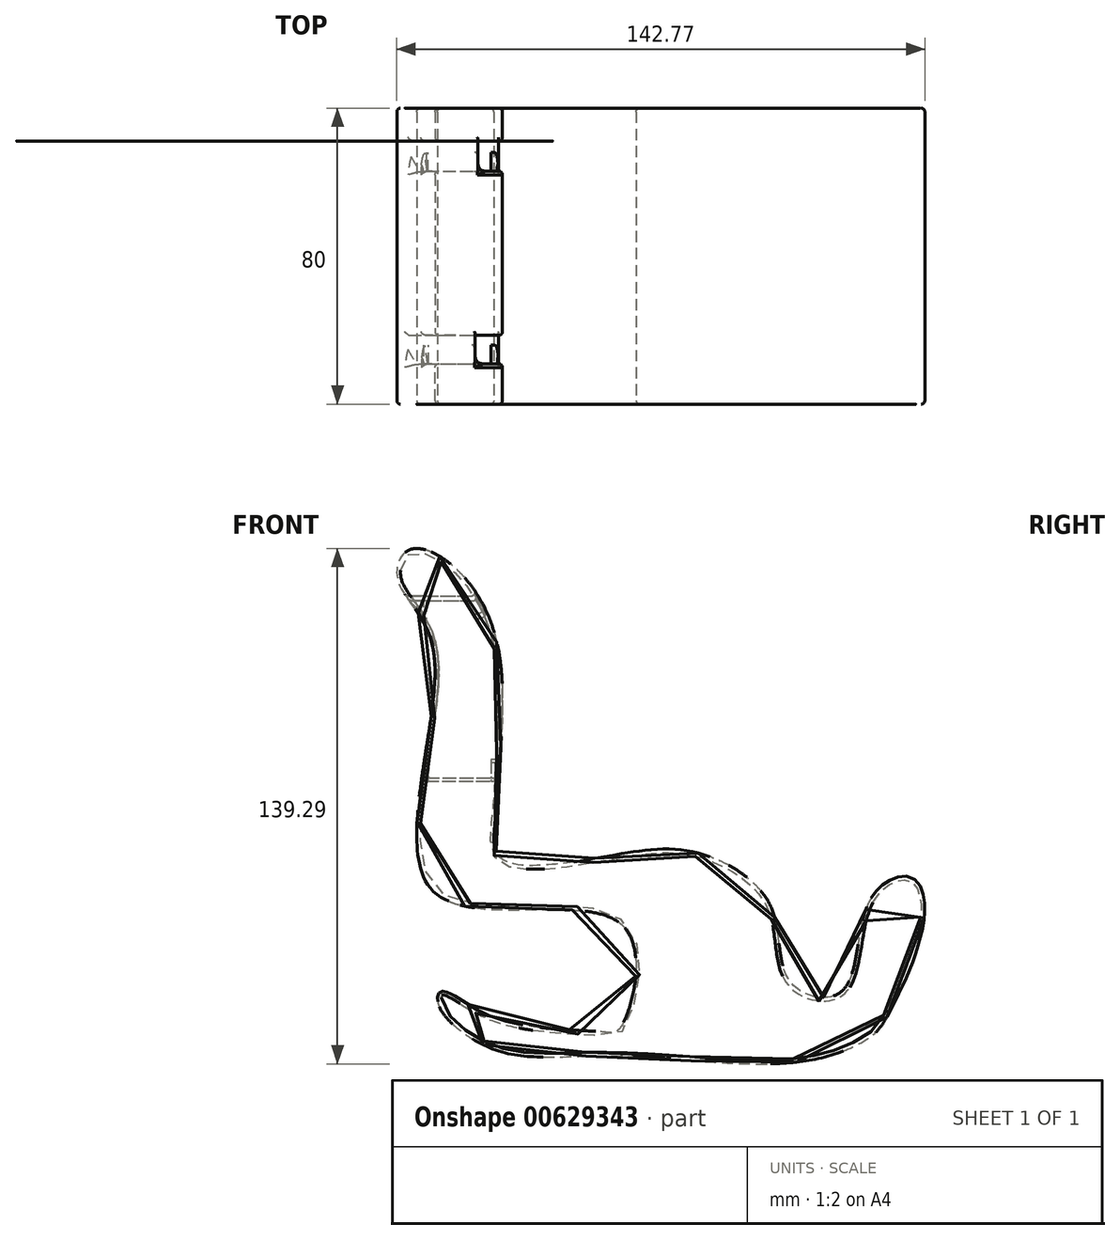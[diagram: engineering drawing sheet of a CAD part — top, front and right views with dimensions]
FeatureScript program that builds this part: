
annotation { "Feature Type Name" : "Feature", "Feature Type Description" : "" }
export const myFeature = defineFeature(function(context is Context, id is Id, definition is map)
    precondition{}
    {
        {
            var Q0;
            Q0=qCreatedBy(makeId("Front.planeOp"),FACE);
            var sketch = newSketch(context, id + "F0", { "sketchPlane" : qUnion([Q0])});
            skFitSpline(sketch, "E0", {"points": [v(60.46, -57.81) * mm, v(55.58, -63.5) * mm, v(36.46, -70.01) * mm, v(-14.39, -68.39) * mm, v(-45.3, -66.76) * mm, v(-60.77, -54.56) * mm, v(-59.95, -50.9) * mm, v(-46.12, -57.81) * mm, v(-16.42, -61.88) * mm, v(-11.54, -60.66) * mm, v(-11.14, -33) * mm, v(-61.99, -24.05) * mm, v(-61.99, 40.23) * mm, v(-71.75, 60.16) * mm, v(-68.9, 68.3) * mm, v(-57.1, 64.23) * mm, v(-44.9, 43.08) * mm, v(-44.09, 12.97) * mm, v(-45.3, -3.7) * mm, v(-43.68, -15.1) * mm, v(-14.39, -14.28) * mm, v(9.2, -13.47) * mm, v(29.14, -28.11) * mm, v(34.43, -48.45) * mm, v(48.26, -50.9) * mm, v(55.58, -26.9) * mm, v(66.56, -19.98) * mm, v(70.63, -30.55) * mm, v(60.46, -57.81) * mm]});
            skSolve(sketch);
        }
        {
            var Q0;
            Q0 = qSketchRegion(id + "F0", true);
            extrude(context, id + "F1", {"entities" : qUnion([Q0]), "endBound" : BoundingType.SYMMETRIC, "oppositeDirection" : true, "depth" : 80 * mm, "offsetDistance" : 25 * mm});
        }
        {
            var Q0;
            Q0=qCreatedBy(makeId("Right.planeOp"),FACE);
            var sketch = newSketch(context, id + "F2", { "sketchPlane" : qUnion([Q0])});
            skLineSegment(sketch, "E1.bottom", {"start": v(-29.09, 55.94) * mm, "end": v(-21.36, 55.94) * mm});
            skLineSegment(sketch, "E1.top", {"start": v(-29.09, 6.71) * mm, "end": v(-21.36, 6.71) * mm});
            skLineSegment(sketch, "E1.left", {"start": v(-29.09, 55.94) * mm, "end": v(-29.09, 6.71) * mm});
            skLineSegment(sketch, "E1.right", {"start": v(-21.36, 55.94) * mm, "end": v(-21.36, 6.71) * mm});
            skSolve(sketch);
        }
        {
            var Q0;
            Q0=qCreatedBy(makeId("Right.planeOp"),FACE);
            var sketch = newSketch(context, id + "F3", { "sketchPlane" : qUnion([Q0])});
            skLineSegment(sketch, "E2.bottom", {"start": v(31.13, 54.72) * mm, "end": v(22.99, 54.72) * mm});
            skLineSegment(sketch, "E2.top", {"start": v(31.13, 5.9) * mm, "end": v(22.99, 5.9) * mm});
            skLineSegment(sketch, "E2.left", {"start": v(31.13, 54.72) * mm, "end": v(31.13, 5.9) * mm});
            skLineSegment(sketch, "E2.right", {"start": v(22.99, 54.72) * mm, "end": v(22.99, 5.9) * mm});
            skSolve(sketch);
        }
        {
            var Q0;
            Q0 = qSketchRegion(id + "F2", true);
            extrude(context, id + "F4", {"entities" : qUnion([Q0]), "operationType" : NewBodyOperationType.REMOVE, "endBound" : BoundingType.THROUGH_ALL, "oppositeDirection" : true, "depth" : 25 * mm, "offsetDistance" : 25 * mm});
        }
        {
            var Q0;
            Q0 = qSketchRegion(id + "F3", true);
            extrude(context, id + "F5", {"entities" : qUnion([Q0]), "operationType" : NewBodyOperationType.REMOVE, "endBound" : BoundingType.THROUGH_ALL, "oppositeDirection" : true, "depth" : 25 * mm, "offsetDistance" : 25 * mm});
        }
        {
            var Q0;
            Q0=makeQuery(id+"F1.opExtrude","CAP_EDGE",EDGE,{"disambiguationData":[OSD([sQuery(id+"F0.wireOp",EDGE,"E0")])],"isStart":true});
            var Q1;
            Q1=makeQuery(id+"F1.opExtrude","CAP_FACE",FACE,{"disambiguationData":[OSD([sQuery(id+"F0.wireOp",EDGE,"E0")])],"isStart":false});
            var Q2;
            Q2=makeQuery(id+"F1.opExtrude","SWEPT_FACE",FACE,{"disambiguationData":[OSD([sQuery(id+"F0.wireOp",EDGE,"E0")])]});
            fillet(context, id + "F6", {"entities" : qUnion([Q0, Q1, Q2]), "radius" : 1 * mm, "tangentPropagation" : true, "allowEdgeOverflow" : false});
        }
        {
            var Q0;
            {var subQ0=makeQuery(id+"F4.opExtrude","SWEPT_FACE",FACE,{"disambiguationData":[OSD([sQuery(id+"F2.wireOp",EDGE,"E1.left")])]});Q0=makeQuery(id+"F6.opFillet","BLEND_EDGE",EDGE,{"blendedFrom":[makeQuery(id+"F4.boolean.opBoolean","INTERSECT",EDGE,{"disambiguationData":[OD(1.0)],"derivedFrom":[makeQuery(id+"F1.opExtrude","SWEPT_FACE",FACE,{"disambiguationData":[OSD([sQuery(id+"F0.wireOp",EDGE,"E0")])]}),subQ0]}),makeQuery(id+"F4.boolean.opBoolean","COPY",FACE,{"derivedFrom":subQ0})],"blendedInto":[makeQuery(id+"F4.boolean.opBoolean","COPY",FACE,{"derivedFrom":subQ0})]});}
            var Q1;
            {var subQ0=makeQuery(id+"F1.opExtrude","SWEPT_FACE",FACE,{"disambiguationData":[OSD([sQuery(id+"F0.wireOp",EDGE,"E0")])]});Q1=makeQuery(id+"F6.opFillet","BLEND_EDGE",EDGE,{"blendedFrom":[makeQuery(id+"F4.boolean.opBoolean","INTERSECT",EDGE,{"disambiguationData":[OD(1.0)],"derivedFrom":[subQ0,makeQuery(id+"F4.opExtrude","SWEPT_FACE",FACE,{"disambiguationData":[OSD([sQuery(id+"F2.wireOp",EDGE,"E1.right")])]})]}),subQ0],"blendedInto":[subQ0]});}
            var Q2;
            {var subQ0=makeQuery(id+"F5.opExtrude","SWEPT_FACE",FACE,{"disambiguationData":[OSD([sQuery(id+"F3.wireOp",EDGE,"E2.right")])]});Q2=makeQuery(id+"F6.opFillet","BLEND_EDGE",EDGE,{"blendedFrom":[makeQuery(id+"F5.boolean.opBoolean","INTERSECT",EDGE,{"disambiguationData":[OD(1.0)],"derivedFrom":[makeQuery(id+"F1.opExtrude","SWEPT_FACE",FACE,{"disambiguationData":[OSD([sQuery(id+"F0.wireOp",EDGE,"E0")])]}),subQ0]}),makeQuery(id+"F5.boolean.opBoolean","COPY",FACE,{"derivedFrom":subQ0})],"blendedInto":[makeQuery(id+"F5.boolean.opBoolean","COPY",FACE,{"derivedFrom":subQ0})]});}
            var Q3;
            {var subQ0=makeQuery(id+"F1.opExtrude","SWEPT_FACE",FACE,{"disambiguationData":[OSD([sQuery(id+"F0.wireOp",EDGE,"E0")])]});Q3=makeQuery(id+"F6.opFillet","BLEND_EDGE",EDGE,{"blendedFrom":[makeQuery(id+"F5.boolean.opBoolean","INTERSECT",EDGE,{"disambiguationData":[OD(1.0)],"derivedFrom":[subQ0,makeQuery(id+"F5.opExtrude","SWEPT_FACE",FACE,{"disambiguationData":[OSD([sQuery(id+"F3.wireOp",EDGE,"E2.left")])]})]}),subQ0],"blendedInto":[subQ0]});}
            var Q4;
            {var subQ0=makeQuery(id+"F5.opExtrude","SWEPT_FACE",FACE,{"disambiguationData":[OSD([sQuery(id+"F3.wireOp",EDGE,"E2.bottom")])]});Q4=makeQuery(id+"F6.opFillet","BLEND_EDGE",EDGE,{"blendedFrom":[makeQuery(id+"F5.boolean.opBoolean","INTERSECT",EDGE,{"disambiguationData":[OD(1.0)],"derivedFrom":[makeQuery(id+"F1.opExtrude","SWEPT_FACE",FACE,{"disambiguationData":[OSD([sQuery(id+"F0.wireOp",EDGE,"E0")])]}),subQ0]}),makeQuery(id+"F5.boolean.opBoolean","COPY",FACE,{"derivedFrom":subQ0})],"blendedInto":[makeQuery(id+"F5.boolean.opBoolean","COPY",FACE,{"derivedFrom":subQ0})]});}
            var Q5;
            {var subQ0=makeQuery(id+"F1.opExtrude","SWEPT_FACE",FACE,{"disambiguationData":[OSD([sQuery(id+"F0.wireOp",EDGE,"E0")])]});Q5=makeQuery(id+"F6.opFillet","BLEND_EDGE",EDGE,{"blendedFrom":[makeQuery(id+"F5.boolean.opBoolean","INTERSECT",EDGE,{"disambiguationData":[OD(1.0)],"derivedFrom":[subQ0,makeQuery(id+"F5.opExtrude","SWEPT_FACE",FACE,{"disambiguationData":[OSD([sQuery(id+"F3.wireOp",EDGE,"E2.top")])]})]}),subQ0],"blendedInto":[subQ0]});}
            var Q6;
            {var subQ0=makeQuery(id+"F1.opExtrude","SWEPT_FACE",FACE,{"disambiguationData":[OSD([sQuery(id+"F0.wireOp",EDGE,"E0")])]});Q6=makeQuery(id+"F6.opFillet","BLEND_EDGE",EDGE,{"blendedFrom":[makeQuery(id+"F4.boolean.opBoolean","INTERSECT",EDGE,{"disambiguationData":[OD(1.0)],"derivedFrom":[subQ0,makeQuery(id+"F4.opExtrude","SWEPT_FACE",FACE,{"disambiguationData":[OSD([sQuery(id+"F2.wireOp",EDGE,"E1.top")])]})]}),subQ0],"blendedInto":[subQ0]});}
            var Q7;
            {var subQ0=makeQuery(id+"F1.opExtrude","SWEPT_FACE",FACE,{"disambiguationData":[OSD([sQuery(id+"F0.wireOp",EDGE,"E0")])]});Q7=makeQuery(id+"F6.opFillet","BLEND_EDGE",EDGE,{"blendedFrom":[makeQuery(id+"F4.boolean.opBoolean","INTERSECT",EDGE,{"disambiguationData":[OD(1.0)],"derivedFrom":[subQ0,makeQuery(id+"F4.opExtrude","SWEPT_FACE",FACE,{"disambiguationData":[OSD([sQuery(id+"F2.wireOp",EDGE,"E1.bottom")])]})]}),subQ0],"blendedInto":[subQ0]});}
            var Q8;
            {var subQ0=makeQuery(id+"F1.opExtrude","SWEPT_FACE",FACE,{"disambiguationData":[OSD([sQuery(id+"F0.wireOp",EDGE,"E0")])]});Q8=makeQuery(id+"F6.opFillet","BLEND_EDGE",EDGE,{"blendedFrom":[makeQuery(id+"F5.boolean.opBoolean","INTERSECT",EDGE,{"disambiguationData":[OD(1.0)],"derivedFrom":[subQ0,makeQuery(id+"F5.opExtrude","SWEPT_FACE",FACE,{"disambiguationData":[OSD([sQuery(id+"F3.wireOp",EDGE,"E2.bottom")])]})]}),subQ0],"blendedInto":[subQ0]});}
            var Q9;
            {var subQ0=makeQuery(id+"F4.opExtrude","SWEPT_FACE",FACE,{"disambiguationData":[OSD([sQuery(id+"F2.wireOp",EDGE,"E1.top")])]});Q9=makeQuery(id+"F6.opFillet","BLEND_EDGE",EDGE,{"blendedFrom":[makeQuery(id+"F4.boolean.opBoolean","INTERSECT",EDGE,{"disambiguationData":[OD(1.0)],"derivedFrom":[makeQuery(id+"F1.opExtrude","SWEPT_FACE",FACE,{"disambiguationData":[OSD([sQuery(id+"F0.wireOp",EDGE,"E0")])]}),subQ0]}),makeQuery(id+"F4.boolean.opBoolean","COPY",FACE,{"derivedFrom":subQ0})],"blendedInto":[makeQuery(id+"F4.boolean.opBoolean","COPY",FACE,{"derivedFrom":subQ0})]});}
            var Q10;
            Q10=makeQuery(id+"F5.boolean.opBoolean","COPY",EDGE,{"derivedFrom":makeQuery(id+"F5.opExtrude","SWEPT_EDGE",EDGE,{"disambiguationData":[OSD([sQuery(id+"F3.wireOp",EDGE,"E2.top"),sQuery(id+"F3.wireOp",EDGE,"E2.right")])]})});
            var Q11;
            {var subQ0=makeQuery(id+"F4.opExtrude","SWEPT_FACE",FACE,{"disambiguationData":[OSD([sQuery(id+"F2.wireOp",EDGE,"E1.bottom")])]});Q11=makeQuery(id+"F6.opFillet","BLEND_EDGE",EDGE,{"blendedFrom":[makeQuery(id+"F4.boolean.opBoolean","INTERSECT",EDGE,{"disambiguationData":[OD(0.0)],"derivedFrom":[makeQuery(id+"F1.opExtrude","SWEPT_FACE",FACE,{"disambiguationData":[OSD([sQuery(id+"F0.wireOp",EDGE,"E0")])]}),subQ0]}),makeQuery(id+"F4.boolean.opBoolean","COPY",FACE,{"derivedFrom":subQ0})],"blendedInto":[makeQuery(id+"F4.boolean.opBoolean","COPY",FACE,{"derivedFrom":subQ0})]});}
            var Q12;
            Q12=makeQuery(id+"F4.boolean.opBoolean","COPY",EDGE,{"derivedFrom":makeQuery(id+"F4.opExtrude","SWEPT_EDGE",EDGE,{"disambiguationData":[OSD([sQuery(id+"F2.wireOp",EDGE,"E1.bottom"),sQuery(id+"F2.wireOp",EDGE,"E1.left")])]})});
            var Q13;
            {var subQ0=makeQuery(id+"F1.opExtrude","SWEPT_FACE",FACE,{"disambiguationData":[OSD([sQuery(id+"F0.wireOp",EDGE,"E0")])]});Q13=makeQuery(id+"F6.opFillet","BLEND_EDGE",EDGE,{"blendedFrom":[makeQuery(id+"F4.boolean.opBoolean","INTERSECT",EDGE,{"disambiguationData":[OD(0.0)],"derivedFrom":[subQ0,makeQuery(id+"F4.opExtrude","SWEPT_FACE",FACE,{"disambiguationData":[OSD([sQuery(id+"F2.wireOp",EDGE,"E1.bottom")])]})]}),subQ0],"blendedInto":[subQ0]});}
            var Q14;
            {var subQ0=makeQuery(id+"F1.opExtrude","SWEPT_FACE",FACE,{"disambiguationData":[OSD([sQuery(id+"F0.wireOp",EDGE,"E0")])]});Q14=makeQuery(id+"F6.opFillet","BLEND_EDGE",EDGE,{"blendedFrom":[makeQuery(id+"F4.boolean.opBoolean","INTERSECT",EDGE,{"disambiguationData":[OD(0.0)],"derivedFrom":[subQ0,makeQuery(id+"F4.opExtrude","SWEPT_FACE",FACE,{"disambiguationData":[OSD([sQuery(id+"F2.wireOp",EDGE,"E1.top")])]})]}),subQ0],"blendedInto":[subQ0]});}
            var Q15;
            {var subQ0=makeQuery(id+"F1.opExtrude","SWEPT_FACE",FACE,{"disambiguationData":[OSD([sQuery(id+"F0.wireOp",EDGE,"E0")])]});Q15=makeQuery(id+"F6.opFillet","BLEND_EDGE",EDGE,{"blendedFrom":[makeQuery(id+"F4.boolean.opBoolean","INTERSECT",EDGE,{"disambiguationData":[OD(0.0)],"derivedFrom":[subQ0,makeQuery(id+"F4.opExtrude","SWEPT_FACE",FACE,{"disambiguationData":[OSD([sQuery(id+"F2.wireOp",EDGE,"E1.left")])]})]}),subQ0],"blendedInto":[subQ0]});}
            var Q16;
            {var subQ0=makeQuery(id+"F5.opExtrude","SWEPT_FACE",FACE,{"disambiguationData":[OSD([sQuery(id+"F3.wireOp",EDGE,"E2.right")])]});Q16=makeQuery(id+"F6.opFillet","BLEND_EDGE",EDGE,{"blendedFrom":[makeQuery(id+"F5.boolean.opBoolean","INTERSECT",EDGE,{"disambiguationData":[OD(0.0)],"derivedFrom":[makeQuery(id+"F1.opExtrude","SWEPT_FACE",FACE,{"disambiguationData":[OSD([sQuery(id+"F0.wireOp",EDGE,"E0")])]}),subQ0]}),makeQuery(id+"F5.boolean.opBoolean","COPY",FACE,{"derivedFrom":subQ0})],"blendedInto":[makeQuery(id+"F5.boolean.opBoolean","COPY",FACE,{"derivedFrom":subQ0})]});}
            var Q17;
            {var subQ0=makeQuery(id+"F1.opExtrude","SWEPT_FACE",FACE,{"disambiguationData":[OSD([sQuery(id+"F0.wireOp",EDGE,"E0")])]});Q17=makeQuery(id+"F6.opFillet","BLEND_EDGE",EDGE,{"blendedFrom":[makeQuery(id+"F5.boolean.opBoolean","INTERSECT",EDGE,{"disambiguationData":[OD(0.0)],"derivedFrom":[subQ0,makeQuery(id+"F5.opExtrude","SWEPT_FACE",FACE,{"disambiguationData":[OSD([sQuery(id+"F3.wireOp",EDGE,"E2.left")])]})]}),subQ0],"blendedInto":[subQ0]});}
            var Q18;
            {var subQ0=makeQuery(id+"F5.opExtrude","SWEPT_FACE",FACE,{"disambiguationData":[OSD([sQuery(id+"F3.wireOp",EDGE,"E2.left")])]});Q18=makeQuery(id+"F6.opFillet","BLEND_EDGE",EDGE,{"blendedFrom":[makeQuery(id+"F5.boolean.opBoolean","INTERSECT",EDGE,{"disambiguationData":[OD(0.0)],"derivedFrom":[makeQuery(id+"F1.opExtrude","SWEPT_FACE",FACE,{"disambiguationData":[OSD([sQuery(id+"F0.wireOp",EDGE,"E0")])]}),subQ0]}),makeQuery(id+"F5.boolean.opBoolean","COPY",FACE,{"derivedFrom":subQ0})],"blendedInto":[makeQuery(id+"F5.boolean.opBoolean","COPY",FACE,{"derivedFrom":subQ0})]});}
            var Q19;
            {var subQ0=makeQuery(id+"F5.opExtrude","SWEPT_FACE",FACE,{"disambiguationData":[OSD([sQuery(id+"F3.wireOp",EDGE,"E2.top")])]});Q19=makeQuery(id+"F6.opFillet","BLEND_EDGE",EDGE,{"blendedFrom":[makeQuery(id+"F5.boolean.opBoolean","INTERSECT",EDGE,{"disambiguationData":[OD(0.0)],"derivedFrom":[makeQuery(id+"F1.opExtrude","SWEPT_FACE",FACE,{"disambiguationData":[OSD([sQuery(id+"F0.wireOp",EDGE,"E0")])]}),subQ0]}),makeQuery(id+"F5.boolean.opBoolean","COPY",FACE,{"derivedFrom":subQ0})],"blendedInto":[makeQuery(id+"F5.boolean.opBoolean","COPY",FACE,{"derivedFrom":subQ0})]});}
            var Q20;
            Q20=makeQuery(id+"F5.boolean.opBoolean","COPY",EDGE,{"derivedFrom":makeQuery(id+"F5.opExtrude","SWEPT_EDGE",EDGE,{"disambiguationData":[OSD([sQuery(id+"F3.wireOp",EDGE,"E2.bottom"),sQuery(id+"F3.wireOp",EDGE,"E2.right")])]})});
            var Q21;
            {var subQ0=makeQuery(id+"F1.opExtrude","SWEPT_FACE",FACE,{"disambiguationData":[OSD([sQuery(id+"F0.wireOp",EDGE,"E0")])]});Q21=makeQuery(id+"F6.opFillet","BLEND_EDGE",EDGE,{"blendedFrom":[makeQuery(id+"F5.boolean.opBoolean","INTERSECT",EDGE,{"disambiguationData":[OD(0.0)],"derivedFrom":[subQ0,makeQuery(id+"F5.opExtrude","SWEPT_FACE",FACE,{"disambiguationData":[OSD([sQuery(id+"F3.wireOp",EDGE,"E2.bottom")])]})]}),subQ0],"blendedInto":[subQ0]});}
            fillet(context, id + "F7", {"entities" : qUnion([Q0, Q1, Q2, Q3, Q4, Q5, Q6, Q7, Q8, Q9, Q10, Q11, Q12, Q13, Q14, Q15, Q16, Q17, Q18, Q19, Q20, Q21]), "radius" : 5 * mm, "tangentPropagation" : true, "allowEdgeOverflow" : false});
        }
        {
            var Q0;
            {var subQ0=makeQuery(id+"F1.opExtrude","SWEPT_FACE",FACE,{"disambiguationData":[OSD([sQuery(id+"F0.wireOp",EDGE,"E0")])]});Q0=makeQuery(id+"F6.opFillet","BLEND_EDGE",EDGE,{"blendedFrom":[makeQuery(id+"F4.boolean.opBoolean","INTERSECT",EDGE,{"disambiguationData":[OD(1.0)],"derivedFrom":[subQ0,makeQuery(id+"F4.opExtrude","SWEPT_FACE",FACE,{"disambiguationData":[OSD([sQuery(id+"F2.wireOp",EDGE,"E1.top")])]})]}),subQ0],"blendedInto":[subQ0]});}
            var Q1;
            {var subQ0=makeQuery(id+"F4.opExtrude","SWEPT_FACE",FACE,{"disambiguationData":[OSD([sQuery(id+"F2.wireOp",EDGE,"E1.top")])]});Q1=makeQuery(id+"F6.opFillet","BLEND_EDGE",EDGE,{"blendedFrom":[makeQuery(id+"F4.boolean.opBoolean","INTERSECT",EDGE,{"disambiguationData":[OD(0.0)],"derivedFrom":[makeQuery(id+"F1.opExtrude","SWEPT_FACE",FACE,{"disambiguationData":[OSD([sQuery(id+"F0.wireOp",EDGE,"E0")])]}),subQ0]}),makeQuery(id+"F4.boolean.opBoolean","COPY",FACE,{"derivedFrom":subQ0})],"blendedInto":[makeQuery(id+"F4.boolean.opBoolean","COPY",FACE,{"derivedFrom":subQ0})]});}
            var Q2;
            {var subQ0=makeQuery(id+"F4.opExtrude","SWEPT_FACE",FACE,{"disambiguationData":[OSD([sQuery(id+"F2.wireOp",EDGE,"E1.top")])]});Q2=makeQuery(id+"F6.opFillet","BLEND_EDGE",EDGE,{"blendedFrom":[makeQuery(id+"F4.boolean.opBoolean","INTERSECT",EDGE,{"disambiguationData":[OD(1.0)],"derivedFrom":[makeQuery(id+"F1.opExtrude","SWEPT_FACE",FACE,{"disambiguationData":[OSD([sQuery(id+"F0.wireOp",EDGE,"E0")])]}),subQ0]}),makeQuery(id+"F4.boolean.opBoolean","COPY",FACE,{"derivedFrom":subQ0})],"blendedInto":[makeQuery(id+"F4.boolean.opBoolean","COPY",FACE,{"derivedFrom":subQ0})]});}
            var Q3;
            {var subQ0=makeQuery(id+"F1.opExtrude","SWEPT_FACE",FACE,{"disambiguationData":[OSD([sQuery(id+"F0.wireOp",EDGE,"E0")])]});Q3=makeQuery(id+"F6.opFillet","BLEND_EDGE",EDGE,{"blendedFrom":[makeQuery(id+"F4.boolean.opBoolean","INTERSECT",EDGE,{"disambiguationData":[OD(1.0)],"derivedFrom":[subQ0,makeQuery(id+"F4.opExtrude","SWEPT_FACE",FACE,{"disambiguationData":[OSD([sQuery(id+"F2.wireOp",EDGE,"E1.right")])]})]}),subQ0],"blendedInto":[subQ0]});}
            var Q4;
            Q4=makeQuery(id+"F4.boolean.opBoolean","COPY",EDGE,{"derivedFrom":makeQuery(id+"F4.opExtrude","SWEPT_EDGE",EDGE,{"disambiguationData":[OSD([sQuery(id+"F2.wireOp",EDGE,"E1.top"),sQuery(id+"F2.wireOp",EDGE,"E1.left")])]})});
            fillet(context, id + "F8", {"entities" : qUnion([Q0, Q1, Q2, Q3, Q4]), "radius" : 5 * mm, "tangentPropagation" : true, "allowEdgeOverflow" : false});
        }
    });
